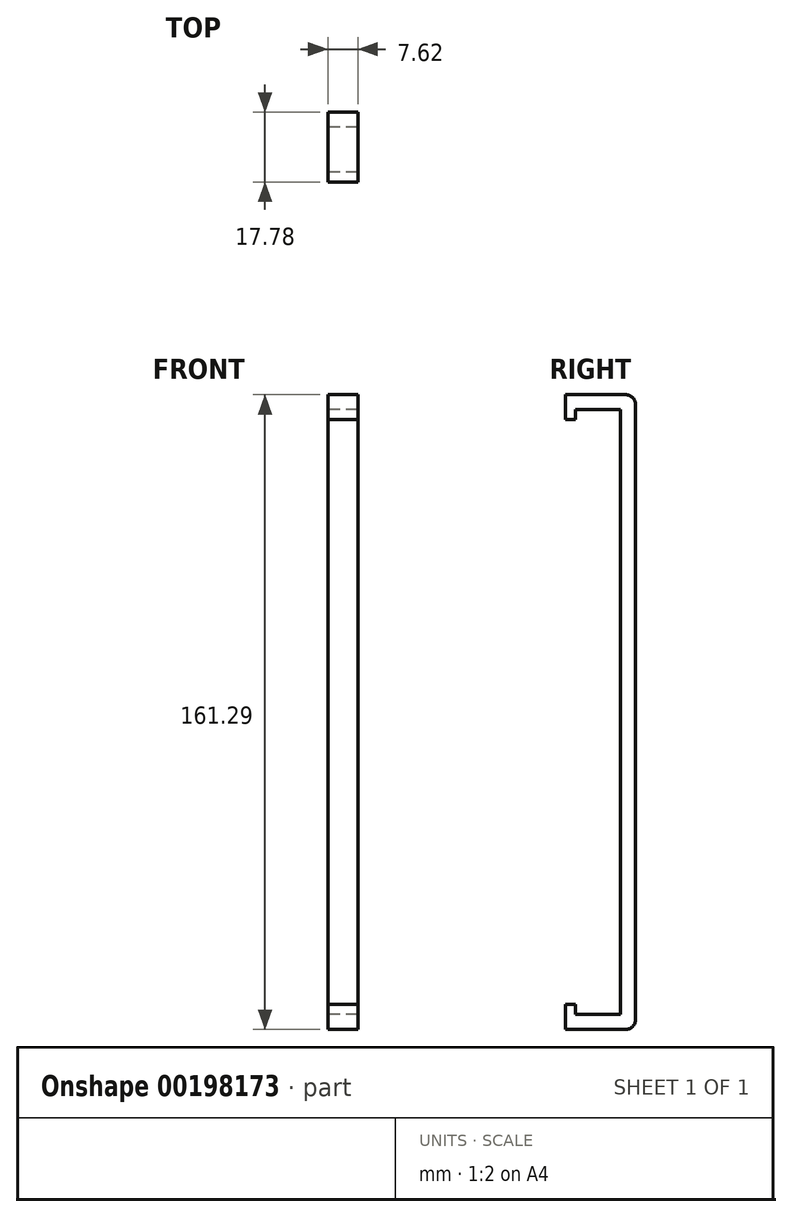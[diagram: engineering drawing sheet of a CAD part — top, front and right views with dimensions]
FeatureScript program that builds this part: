
annotation { "Feature Type Name" : "Feature", "Feature Type Description" : "" }
export const myFeature = defineFeature(function(context is Context, id is Id, definition is map)
    precondition{}
    {
        {
            var Q0;
            Q0=qCreatedBy(makeId("Right.planeOp"),FACE);
            var sketch = newSketch(context, id + "F0", { "sketchPlane" : qUnion([Q0])});
            skLineSegment(sketch, "E0", {"start": v(-21.61, -75.1) * mm, "end": v(-21.61, 86.2) * mm});
            skLineSegment(sketch, "E1", {"start": v(-21.61, 86.2) * mm, "end": v(-36.85, 86.2) * mm});
            skLineSegment(sketch, "E2", {"start": v(-36.85, 82.39) * mm, "end": v(-25.42, 82.39) * mm});
            skLineSegment(sketch, "E3", {"start": v(-25.42, 82.39) * mm, "end": v(-25.42, -71.28) * mm});
            skLineSegment(sketch, "E4", {"start": v(-25.42, -71.28) * mm, "end": v(-36.85, -71.28) * mm});
            skLineSegment(sketch, "E5", {"start": v(-36.85, -71.28) * mm, "end": v(-36.85, -68.74) * mm});
            skLineSegment(sketch, "E6", {"start": v(-15.6, -75.1) * mm, "end": v(-39.4, -75.1) * mm});
            skLineSegment(sketch, "E7", {"start": v(-39.4, -75.1) * mm, "end": v(-39.4, -68.74) * mm});
            skLineSegment(sketch, "E8", {"start": v(-39.4, -68.74) * mm, "end": v(-36.85, -68.74) * mm});
            skPoint(sketch, "E9", {"position": v(-21.61, 5.55) * mm});
            skLineSegment(sketch, "E10", {"start": v(-21.61, 5.55) * mm, "end": v(-21.61, 86.2) * mm, "construction": true});
            skPoint(sketch, "E11.visualSharp", {"position": v(-21.61, -75.1) * mm});
            skLineSegment(sketch, "E12", {"start": v(-21.61, -75.1) * mm, "end": v(-15.6, -75.1) * mm});
            skLineSegment(sketch, "E13.bottom", {"start": v(-36.85, 86.2) * mm, "end": v(-39.4, 86.2) * mm});
            skLineSegment(sketch, "E13.top", {"start": v(-36.85, 79.85) * mm, "end": v(-39.4, 79.85) * mm});
            skLineSegment(sketch, "E13.left", {"start": v(-36.85, 82.39) * mm, "end": v(-36.85, 79.85) * mm});
            skLineSegment(sketch, "E13.right", {"start": v(-39.4, 86.2) * mm, "end": v(-39.4, 79.85) * mm});
            skSolve(sketch);
        }
        {
            var Q0;
            {var subQ4=sQuery(id+"F0.wireOp",EDGE,"E1");Q0=makeQuery(id+"F0.imprint","IMPRINT",FACE,{"disambiguationData":[TD([[makeQuery(id+"F0.imprint","IMPRINT",EDGE,{"derivedFrom":subQ4}),1.0]])]});}
            var Q1;
            Q1=makeQuery(id+"F0.imprint","IMPRINT",FACE,{"disambiguationData":[TD([[makeQuery(id+"F0.imprint","IMPRINT",EDGE,{"derivedFrom":sQuery(id+"F0.wireOp",EDGE,"GniolQ8k-1lFO-syOV-Kmio-4kkoYGTirxtP")}),-1.0]])]});
            extrude(context, id + "F1", {"entities" : qUnion([Q0, Q1]), "depth" : 7.62 * mm});
        }
        {
            var Q0;
            Q0=makeQuery(id+"F1.opExtrude","SWEPT_EDGE",EDGE,{"disambiguationData":[OSD([sQuery(id+"F0.wireOp",EDGE,"E0"),sQuery(id+"F0.wireOp",EDGE,"t3ux4Hx8-J6N8-xwGX-sIUz-kl5DJuyon6PA")])]});
            var Q1;
            Q1=makeQuery(id+"F1.opExtrude","SWEPT_EDGE",EDGE,{"disambiguationData":[OSD([sQuery(id+"F0.wireOp",EDGE,"uGzN4Soo-Qp1Y-qerp-QgII-JUOMiOSDvkiM"),sQuery(id+"F0.wireOp",EDGE,"t3ux4Hx8-J6N8-xwGX-sIUz-kl5DJuyon6PA")])]});
            fillet(context, id + "F2", {"entities" : qUnion([Q0, Q1]), "radius" : 2.54 * mm, "tangentPropagation" : true, "allowEdgeOverflow" : false});
        }
    });
